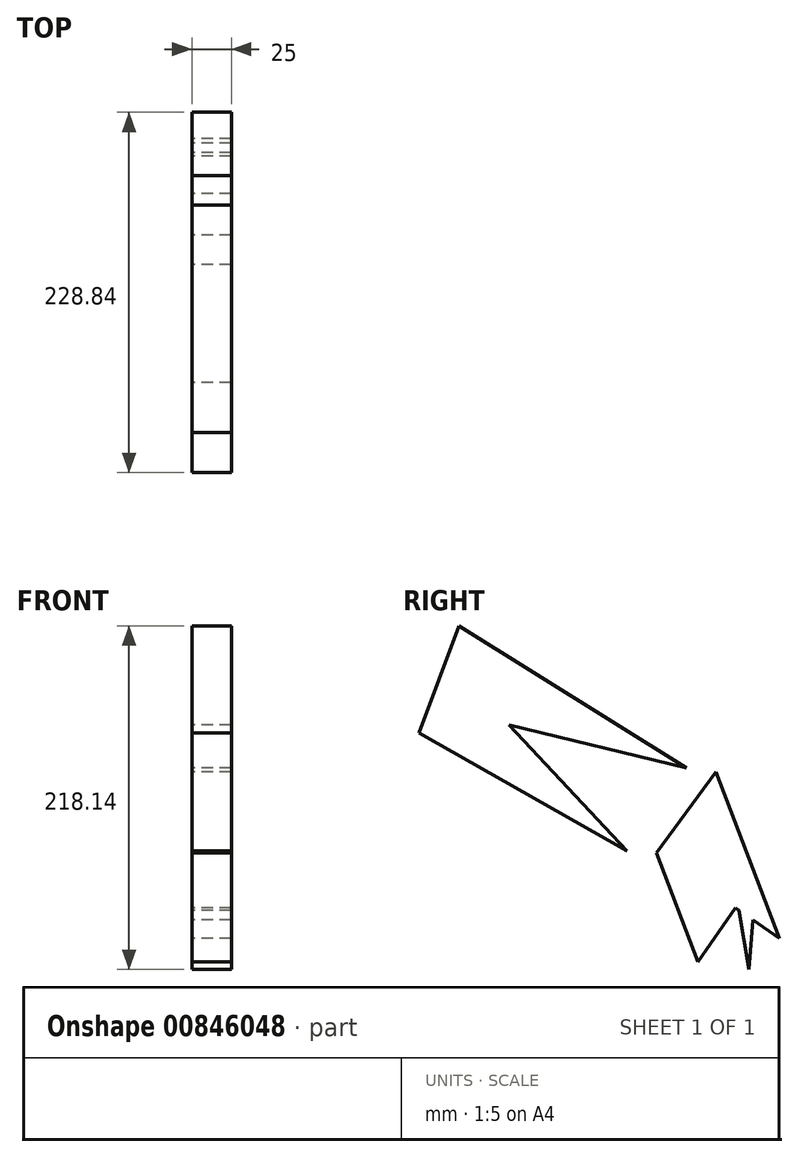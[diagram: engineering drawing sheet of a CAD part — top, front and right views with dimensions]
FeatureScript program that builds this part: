
annotation { "Feature Type Name" : "Feature", "Feature Type Description" : "" }
export const myFeature = defineFeature(function(context is Context, id is Id, definition is map)
    precondition{}
    {
        {
            var Q0;
            Q0=qCreatedBy(makeId("Right.planeOp"),FACE);
            var sketch = newSketch(context, id + "F0", { "sketchPlane" : qUnion([Q0])});
            skLineSegment(sketch, "E0", {"start": v(-22.99, 40.76) * mm, "end": v(34.08, -29.02) * mm});
            skLineSegment(sketch, "E1", {"start": v(34.08, -29.02) * mm, "end": v(-43.53, -20.87) * mm});
            skLineSegment(sketch, "E2", {"start": v(-43.53, -20.87) * mm, "end": v(30.16, 45) * mm});
            skLineSegment(sketch, "E3", {"start": v(30.16, 45) * mm, "end": v(34.08, -29.02) * mm});
            skLineSegment(sketch, "E4", {"start": v(-22.99, 40.76) * mm, "end": v(0, 61.3) * mm});
            skLineSegment(sketch, "E5", {"start": v(0, 61.3) * mm, "end": v(30.16, 45) * mm});
            skLineSegment(sketch, "E6", {"start": v(-22.99, 40.76) * mm, "end": v(-46.23, 19.99) * mm});
            skLineSegment(sketch, "E7", {"start": v(-46.23, 19.99) * mm, "end": v(-43.53, -20.87) * mm});
            skLineSegment(sketch, "E8.bottom", {"start": v(-33.1, 19.99) * mm, "end": v(-21.03, 19.99) * mm});
            skLineSegment(sketch, "E8.top", {"start": v(-33.1, 14.35) * mm, "end": v(-21.03, 14.35) * mm});
            skLineSegment(sketch, "E8.left", {"start": v(-33.1, 19.99) * mm, "end": v(-33.1, 14.35) * mm});
            skLineSegment(sketch, "E8.right", {"start": v(-21.03, 19.99) * mm, "end": v(-21.03, 14.35) * mm});
            skLineSegment(sketch, "E9", {"start": v(30.16, 45) * mm, "end": v(120.6, 17.6) * mm});
            skLineSegment(sketch, "E10", {"start": v(120.6, 17.6) * mm, "end": v(34.08, -29.02) * mm});
            skLineSegment(sketch, "E11", {"start": v(-22.99, 40.76) * mm, "end": v(135.35, -8.48) * mm});
            skLineSegment(sketch, "E12", {"start": v(135.35, -8.48) * mm, "end": v(93.1, -46.25) * mm});
            skLineSegment(sketch, "E13", {"start": v(93.1, -46.25) * mm, "end": v(30.16, 45) * mm});
            skLineSegment(sketch, "E14", {"start": v(120.6, 17.6) * mm, "end": v(109.06, 62.28) * mm});
            skLineSegment(sketch, "E15", {"start": v(109.06, 62.28) * mm, "end": v(30.16, 45) * mm});
            skLineSegment(sketch, "E16", {"start": v(34.08, -29.02) * mm, "end": v(73.55, 22.5) * mm});
            skLineSegment(sketch, "E17", {"start": v(73.55, 22.5) * mm, "end": v(-43.53, -20.87) * mm});
            skLineSegment(sketch, "E18", {"start": v(70.5, 21.37) * mm, "end": v(109.06, 62.28) * mm});
            skLineSegment(sketch, "E19", {"start": v(73.55, 22.5) * mm, "end": v(120.6, 17.6) * mm});
            skLineSegment(sketch, "E20", {"start": v(70.5, 21.37) * mm, "end": v(30.16, 45) * mm});
            skSolve(sketch);
        }
        {
            var Q0;
            Q0=qCreatedBy(makeId("Right.planeOp"),FACE);
            var sketch = newSketch(context, id + "F1", { "sketchPlane" : qUnion([Q0])});
            skLineSegment(sketch, "E21", {"start": v(70.34, 21.81) * mm, "end": v(110.7, -84.07) * mm});
            skLineSegment(sketch, "E22", {"start": v(110.7, -84.07) * mm, "end": v(32.7, -29.86) * mm});
            skLineSegment(sketch, "E23", {"start": v(32.7, -29.86) * mm, "end": v(70.34, 21.81) * mm});
            skLineSegment(sketch, "E24", {"start": v(32.7, -29.86) * mm, "end": v(59.04, -98.83) * mm});
            skLineSegment(sketch, "E25", {"start": v(59.04, -98.83) * mm, "end": v(96.03, -45.6) * mm});
            skLineSegment(sketch, "E26", {"start": v(96.03, -45.6) * mm, "end": v(91.15, -103.76) * mm});
            skLineSegment(sketch, "E27", {"start": v(91.15, -103.76) * mm, "end": v(70.34, 21.81) * mm});
            skSolve(sketch);
        }
        {
            var Q0;
            Q0 = qSketchRegion(id + "F1", true);
            extrude(context, id + "F2", {"entities" : qUnion([Q0]), "depth" : 25 * mm, "offsetDistance" : 25 * mm});
        }
        {
            var Q0;
            {var subQ1=sQuery(id+"F0.wireOp",EDGE,"E2");var subQ7=sQuery(id+"F0.wireOp",EDGE,"E0");var subQ8=makeQuery(id+"F0.imprint","INTERSECT",VERTEX,{"derivedFrom":[subQ7,subQ1]});Q0=makeQuery(id+"F0.imprint","IMPRINT",FACE,{"disambiguationData":[TD([[makeQuery(id+"F0.imprint","IMPRINT",EDGE,{"disambiguationData":[TD([[subQ8,-1.0]])],"derivedFrom":subQ7}),1.0]])]});}
            var sketch = newSketch(context, id + "F3", { "sketchPlane" : qUnion([Q0])});
            skLineSegment(sketch, "E28", {"start": v(51.64, 24.18) * mm, "end": v(-92.7, 114.38) * mm});
            skLineSegment(sketch, "E29", {"start": v(-92.7, 114.38) * mm, "end": v(-118.14, 46.43) * mm});
            skLineSegment(sketch, "E30", {"start": v(-118.14, 46.43) * mm, "end": v(13.97, -28.55) * mm});
            skLineSegment(sketch, "E31", {"start": v(13.97, -28.55) * mm, "end": v(-61.07, 51.42) * mm});
            skLineSegment(sketch, "E32", {"start": v(-61.07, 51.42) * mm, "end": v(51.64, 24.18) * mm});
            skLineSegment(sketch, "E33", {"start": v(-61.07, 51.42) * mm, "end": v(-92.7, 114.38) * mm});
            skLineSegment(sketch, "E34", {"start": v(-61.07, 51.42) * mm, "end": v(-118.14, 46.43) * mm});
            skSolve(sketch);
        }
        {
            var Q0;
            Q0 = qSketchRegion(id + "F3", true);
            extrude(context, id + "F4", {"entities" : qUnion([Q0]), "depth" : 25 * mm, "offsetDistance" : 25 * mm});
        }
    });
